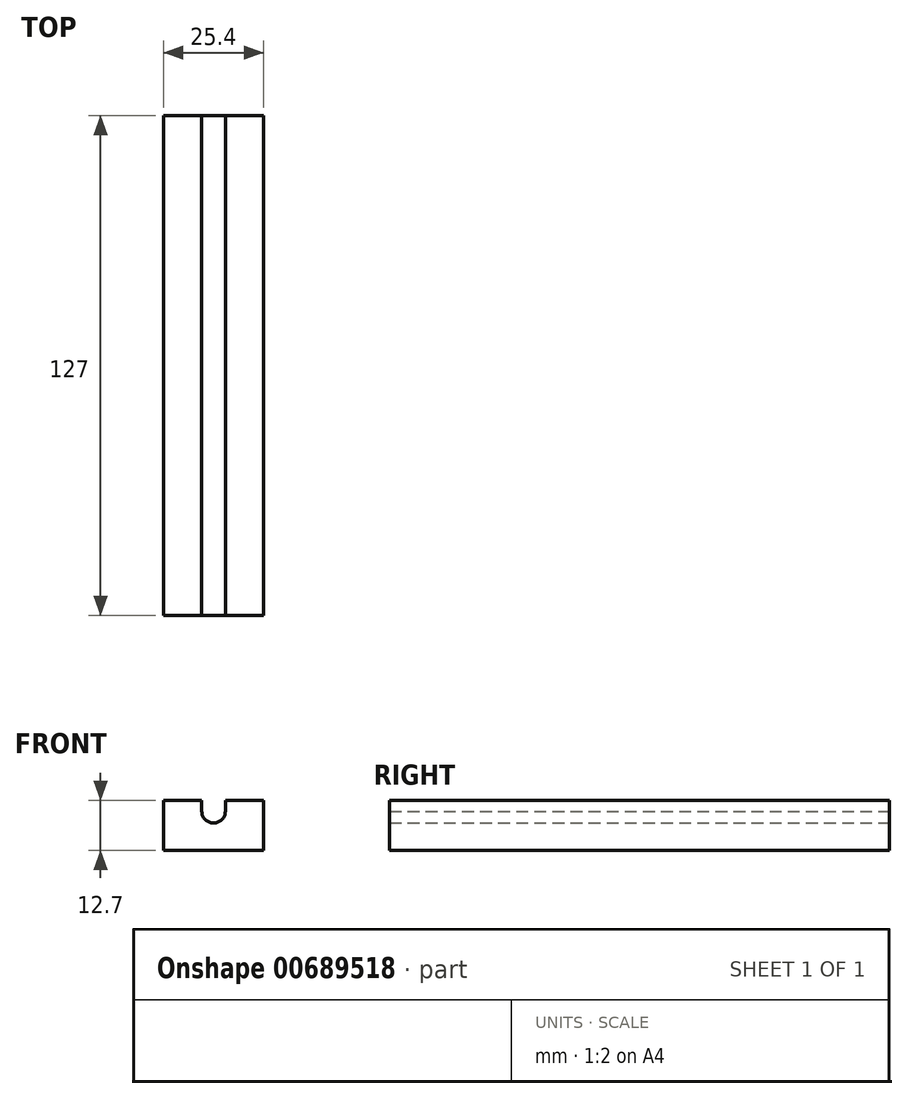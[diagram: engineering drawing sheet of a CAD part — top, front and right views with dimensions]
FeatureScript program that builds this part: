
annotation { "Feature Type Name" : "Feature", "Feature Type Description" : "" }
export const myFeature = defineFeature(function(context is Context, id is Id, definition is map)
    precondition{}
    {
        {
            var Q0;
            Q0=qCreatedBy(makeId("Front.planeOp"),FACE);
            var sketch = newSketch(context, id + "F0", { "sketchPlane" : qUnion([Q0])});
            skCircle(sketch, "E0", {"center": v(0, 58.21) * mm, "radius": 3 * mm});
            skLineSegment(sketch, "E1.bottom", {"start": v(3, 58.21) * mm, "end": v(-3.01, 58.21) * mm});
            skLineSegment(sketch, "E1.top", {"start": v(3, 63.47) * mm, "end": v(-3.01, 63.47) * mm});
            skLineSegment(sketch, "E1.left", {"start": v(3, 58.21) * mm, "end": v(3, 63.47) * mm});
            skLineSegment(sketch, "E1.right", {"start": v(-3.01, 58.21) * mm, "end": v(-3.01, 63.47) * mm});
            skLineSegment(sketch, "E2.bottom", {"start": v(-12.7, 60.96) * mm, "end": v(12.7, 60.96) * mm});
            skLineSegment(sketch, "E2.top", {"start": v(-12.7, 48.26) * mm, "end": v(12.7, 48.26) * mm});
            skLineSegment(sketch, "E2.left", {"start": v(-12.7, 60.96) * mm, "end": v(-12.7, 48.26) * mm});
            skLineSegment(sketch, "E2.right", {"start": v(12.7, 60.96) * mm, "end": v(12.7, 48.26) * mm});
            skSolve(sketch);
        }
        {
            var Q0;
            Q0=makeQuery(id+"F0.imprint","IMPRINT",FACE,{"disambiguationData":[TD([[makeQuery(id+"F0.imprint","IMPRINT",EDGE,{"derivedFrom":sQuery(id+"F0.wireOp",EDGE,"E2.top")}),1.0]])]});
            extrude(context, id + "F1", {"entities" : qUnion([Q0]), "depth" : 127 * mm, "offsetDistance" : 25.4 * mm});
        }
    });
